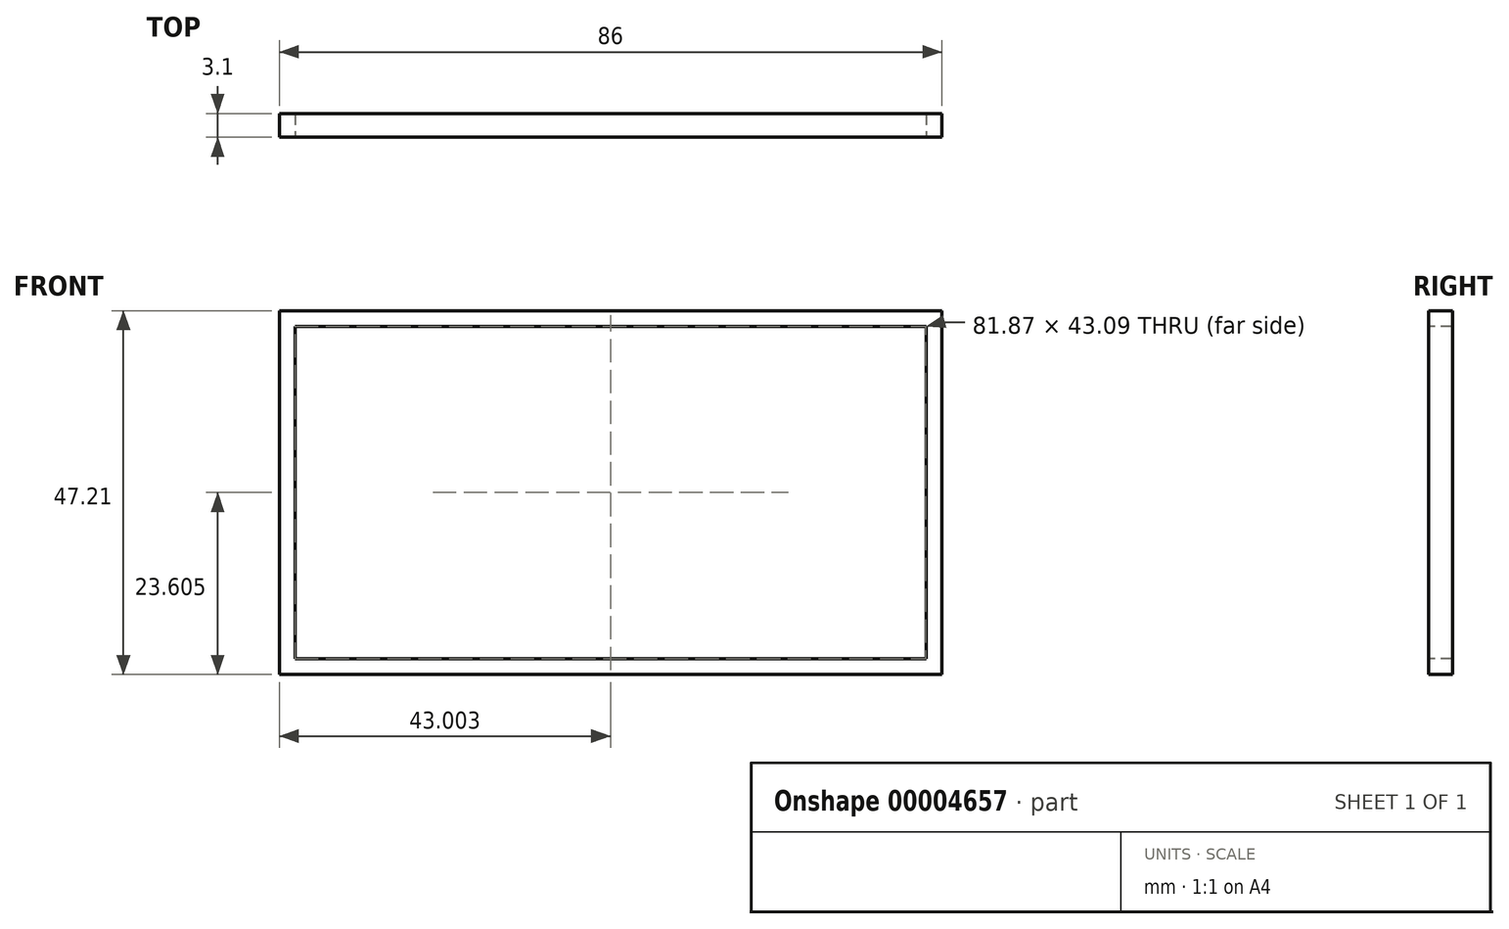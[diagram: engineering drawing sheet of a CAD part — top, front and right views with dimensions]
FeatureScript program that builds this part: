
annotation { "Feature Type Name" : "Feature", "Feature Type Description" : "" }
export const myFeature = defineFeature(function(context is Context, id is Id, definition is map)
    precondition{}
    {
        {
            var Q0;
            Q0=qCreatedBy(makeId("Front.planeOp"),FACE);
            var sketch = newSketch(context, id + "F0", { "sketchPlane" : qUnion([Q0])});
            skLineSegment(sketch, "E0.bottom", {"start": v(-62.7, 43.02) * mm, "end": v(-14.43, 43.02) * mm});
            skLineSegment(sketch, "E0.top", {"start": v(-62.7, 18.19) * mm, "end": v(-14.43, 18.19) * mm});
            skLineSegment(sketch, "E0.left", {"start": v(-62.7, 43.02) * mm, "end": v(-62.7, 18.19) * mm});
            skLineSegment(sketch, "E0.right", {"start": v(-14.43, 43.02) * mm, "end": v(-14.43, 18.19) * mm});
            skLineSegment(sketch, "E1.bottom", {"start": v(-62.7, 43.02) * mm, "end": v(-78.05, 43.02) * mm});
            skLineSegment(sketch, "E1.top", {"start": v(-62.7, 18.19) * mm, "end": v(-78.05, 18.19) * mm});
            skLineSegment(sketch, "E1.right", {"start": v(-78.05, 43.02) * mm, "end": v(-78.05, 18.19) * mm});
            skSolve(sketch);
        }
        {
            var Q0;
            Q0=qCreatedBy(makeId("Right.planeOp"),FACE);
            var sketch = newSketch(context, id + "F1", { "sketchPlane" : qUnion([Q0])});
            skLineSegment(sketch, "E2.bottom", {"start": v(-36.15, 9.06) * mm, "end": v(-33.05, 9.06) * mm});
            skLineSegment(sketch, "E2.top", {"start": v(-36.15, 7) * mm, "end": v(-33.05, 7) * mm});
            skLineSegment(sketch, "E2.left", {"start": v(-36.15, 9.06) * mm, "end": v(-36.15, 7) * mm});
            skLineSegment(sketch, "E2.right", {"start": v(-33.05, 9.06) * mm, "end": v(-33.05, 7) * mm});
            skSolve(sketch);
        }
        {
            var Q0;
            Q0=makeQuery(id+"F1.imprint","IMPRINT",FACE,{"disambiguationData":[TD([[makeQuery(id+"F1.imprint","IMPRINT",EDGE,{"derivedFrom":sQuery(id+"F1.wireOp",EDGE,"E2.bottom")}),-1.0]])]});
            var Q1;
            Q1=sQuery(id+"F0.wireOp",EDGE,"E0.top");
            var Q2;
            Q2=sQuery(id+"F0.wireOp",EDGE,"E0.right");
            var Q3;
            Q3=sQuery(id+"F0.wireOp",EDGE,"E0.bottom");
            var Q4;
            Q4=sQuery(id+"F0.wireOp",EDGE,"E1.bottom");
            var Q5;
            Q5=sQuery(id+"F0.wireOp",EDGE,"E1.right");
            var Q6;
            Q6=sQuery(id+"F0.wireOp",EDGE,"E1.top");
            sweep(context, id + "F2", {"profiles" : qUnion([Q0]), "path" : qUnion([Q1, Q2, Q3, Q4, Q5, Q6])});
        }
    });
